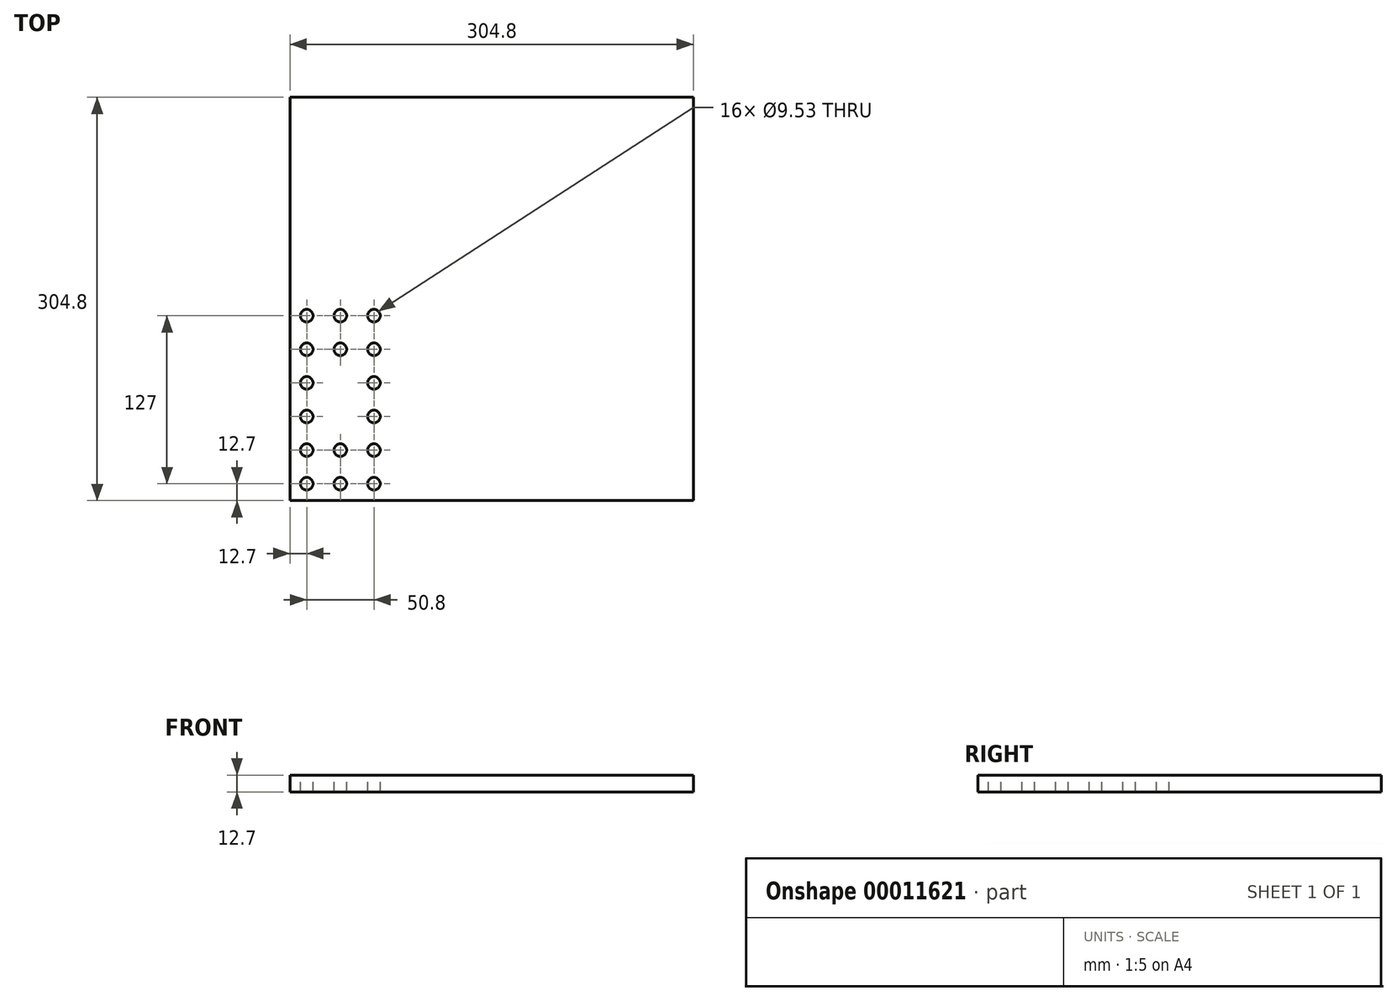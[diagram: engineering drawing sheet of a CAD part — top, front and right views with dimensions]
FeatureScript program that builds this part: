
annotation { "Feature Type Name" : "Feature", "Feature Type Description" : "" }
export const myFeature = defineFeature(function(context is Context, id is Id, definition is map)
    precondition{}
    {
        {
            var Q0;
            Q0=qCreatedBy(makeId("Top.planeOp"),FACE);
            var sketch = newSketch(context, id + "F0", { "sketchPlane" : qUnion([Q0])});
            skLineSegment(sketch, "E0.bottom", {"start": v(0, 0) * mm, "end": v(304.8, 0) * mm});
            skLineSegment(sketch, "E0.top", {"start": v(0, 304.8) * mm, "end": v(304.8, 304.8) * mm});
            skLineSegment(sketch, "E0.left", {"start": v(0, 0) * mm, "end": v(0, 304.8) * mm});
            skLineSegment(sketch, "E0.right", {"start": v(304.8, 0) * mm, "end": v(304.8, 304.8) * mm});
            skSolve(sketch);
        }
        {
            var Q0;
            Q0=makeQuery(id+"F0.imprint","IMPRINT",FACE,{"disambiguationData":[TD([[makeQuery(id+"F0.imprint","IMPRINT",EDGE,{"derivedFrom":sQuery(id+"F0.wireOp",EDGE,"E0.bottom")}),1.0]])]});
            extrude(context, id + "F1", {"entities" : qUnion([Q0]), "oppositeDirection" : true, "depth" : 12.7 * mm});
        }
        {
            var Q0;
            Q0=makeQuery(id+"F1.opExtrude","CAP_FACE",FACE,{"disambiguationData":[OSD([sQuery(id+"F0.wireOp",EDGE,"E0.bottom"),sQuery(id+"F0.wireOp",EDGE,"E0.top"),sQuery(id+"F0.wireOp",EDGE,"E0.left"),sQuery(id+"F0.wireOp",EDGE,"E0.right")])],"isStart":true});
            var sketch = newSketch(context, id + "F2", { "sketchPlane" : qUnion([Q0])});
            skCircle(sketch, "E1", {"center": v(12.7, 12.7) * mm, "radius": 4.76 * mm});
            skCircle(sketch, "E2.0.1.0", {"center": v(12.7, 38.1) * mm, "radius": 4.76 * mm});
            skCircle(sketch, "E2.0.2.0", {"center": v(12.7, 63.5) * mm, "radius": 4.76 * mm});
            skCircle(sketch, "E2.0.3.0", {"center": v(12.7, 88.9) * mm, "radius": 4.76 * mm});
            skCircle(sketch, "E2.0.4.0", {"center": v(12.7, 114.3) * mm, "radius": 4.76 * mm});
            skCircle(sketch, "E2.0.5.0", {"center": v(12.7, 139.7) * mm, "radius": 4.76 * mm});
            skCircle(sketch, "E2.1.0.0", {"center": v(38.1, 12.7) * mm, "radius": 4.76 * mm});
            skCircle(sketch, "E2.1.1.0", {"center": v(38.1, 38.1) * mm, "radius": 4.76 * mm});
            skCircle(sketch, "E2.1.4.0", {"center": v(38.1, 114.3) * mm, "radius": 4.76 * mm});
            skCircle(sketch, "E2.1.5.0", {"center": v(38.1, 139.7) * mm, "radius": 4.76 * mm});
            skCircle(sketch, "E2.2.0.0", {"center": v(63.5, 12.7) * mm, "radius": 4.76 * mm});
            skCircle(sketch, "E2.2.1.0", {"center": v(63.5, 38.1) * mm, "radius": 4.76 * mm});
            skCircle(sketch, "E2.2.2.0", {"center": v(63.5, 63.5) * mm, "radius": 4.76 * mm});
            skCircle(sketch, "E2.2.3.0", {"center": v(63.5, 88.9) * mm, "radius": 4.76 * mm});
            skCircle(sketch, "E2.2.4.0", {"center": v(63.5, 114.3) * mm, "radius": 4.76 * mm});
            skCircle(sketch, "E2.2.5.0", {"center": v(63.5, 139.7) * mm, "radius": 4.76 * mm});
            skLineSegment(sketch, "E2.direction1", {"start": v(12.7, 12.7) * mm, "end": v(38.1, 12.7) * mm, "construction": true});
            skLineSegment(sketch, "E2.direction2", {"start": v(12.7, 12.7) * mm, "end": v(12.7, 38.1) * mm, "construction": true});
            skSolve(sketch);
        }
        {
            var Q0;
            Q0 = qSketchRegion(id + "F2", true);
            extrude(context, id + "F3", {"entities" : qUnion([Q0]), "operationType" : NewBodyOperationType.REMOVE, "endBound" : BoundingType.THROUGH_ALL, "oppositeDirection" : true, "depth" : 25.4 * mm});
        }
    });
